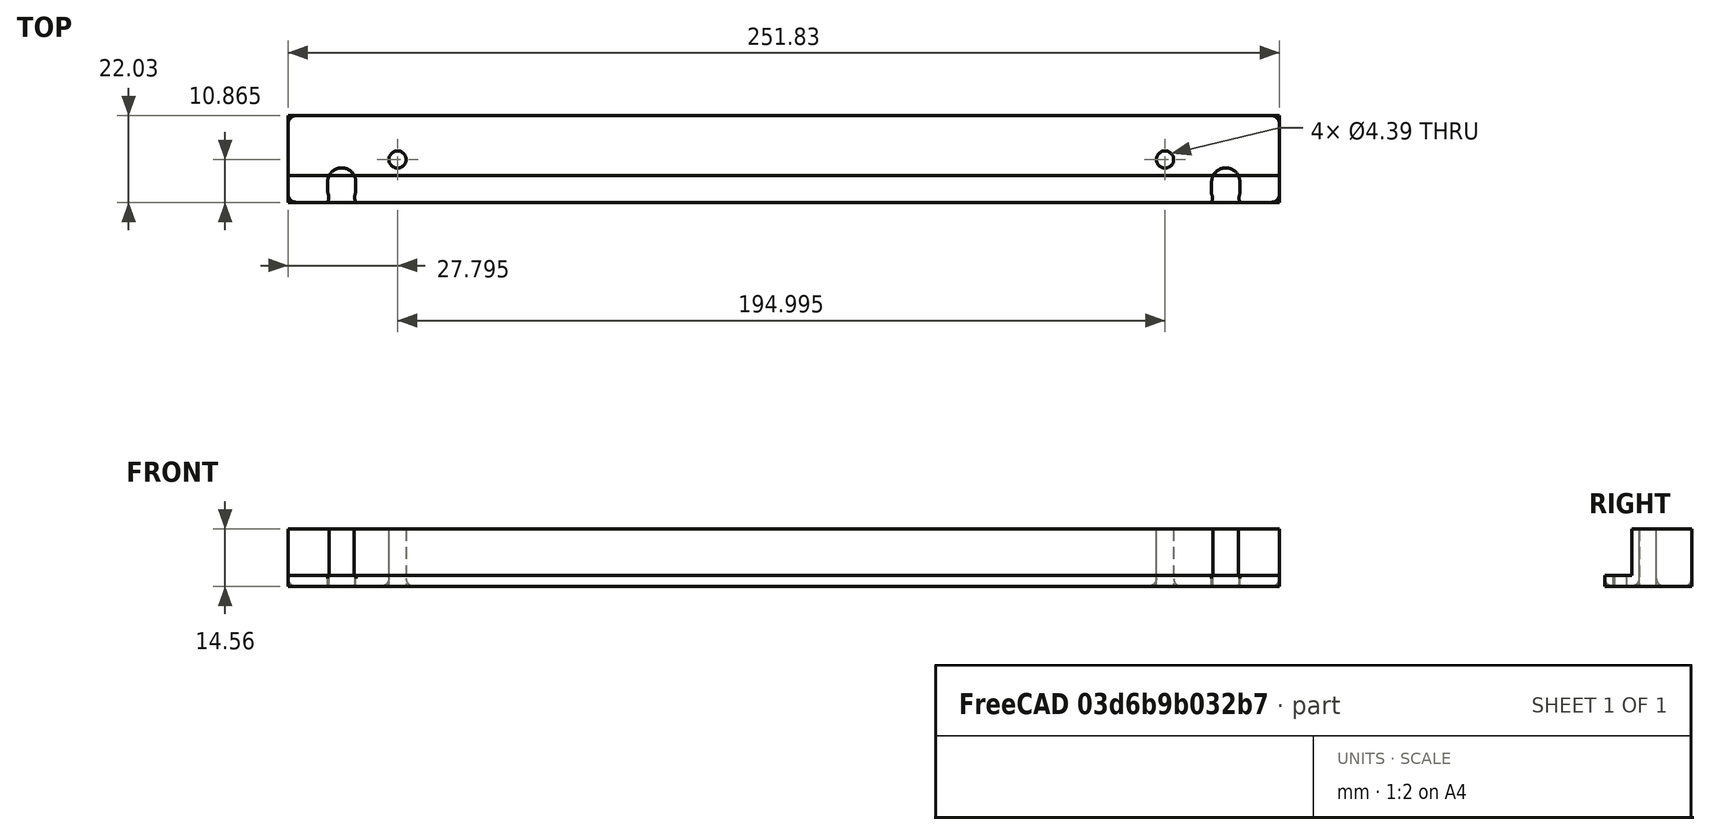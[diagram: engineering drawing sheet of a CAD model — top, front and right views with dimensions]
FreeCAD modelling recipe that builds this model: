
FCSTD DOCUMENT  (FreeCAD 0.19R24276 (Git))
Label: Pieza_Suegros
License: All rights reserved
LicenseURL: http://en.wikipedia.org/wiki/All_rights_reserved
objects: TechDraw::DrawViewDimension×10, Part::Fillet×3, TechDraw::DrawProjGroupItem×3, Part::Box×2, Sketcher::SketchObject×2, PartDesign::Pocket×2, TechDraw::DrawSVGTemplate×2, TechDraw::DrawViewPart×2, TechDraw::DrawPage×2, Part::Cut×1, TechDraw::DrawProjGroup×1, TechDraw::DrawViewAnnotation×1
note: 12 computed .brp shape members not serialized (recipe doc carries the construction recipe); baked Part::Feature solids carry a one-line shape summary decoded from their .brp

FEATURE [Part::Box] Box  label="Cubo"
  AttacherType = Attacher::AttachEngine3D
  Height = 14.56
  Length = 251.83
  Width = 22.03
FEATURE [Part::Box] Box001  label="Cubo001"
  AttacherType = Attacher::AttachEngine3D
  Height = 11.75
  Length = 251.83
  Placement = pos=(0,0,2.81) rot=(0,0,1;0rad)
  Width = 6.77
FEATURE [Part::Cut] Cut
  Base = -> Box
  Tool = -> Box001
FEATURE [Sketcher::SketchObject] Sketch
  ExternalGeometry = -> [Cut]
  FullyConstrained = false
  MapMode = 5
  Placement = pos=(0,0,14.56) rot=(0,0,1;0rad)
  Support = -> [Cut]
  sketch-geometry (6):
    g0: LineSegment StartX=0 StartY=6.77 StartZ=0 EndX=27.795 EndY=6.77 EndZ=0
    g1: LineSegment StartX=27.795 StartY=6.77 StartZ=0 EndX=27.795 EndY=10.865 EndZ=0
    g2: Circle CenterX=27.795 CenterY=10.865 CenterZ=0 NormalX=0 NormalY=0 NormalZ=1 AngleXU=0 Radius=2.195
    g3: LineSegment StartX=251.83 StartY=6.77 StartZ=0 EndX=222.79 EndY=6.77 EndZ=0
    g4: LineSegment StartX=222.79 StartY=6.77 StartZ=0 EndX=222.79 EndY=10.865 EndZ=0
    g5: Circle CenterX=222.79 CenterY=10.865 CenterZ=0 NormalX=0 NormalY=0 NormalZ=1 AngleXU=0 Radius=2.195
  constraints (16):
    c: Coincident(g0,g-3)
    c: Horizontal(g0)
    c: DistanceX(g0) = 27.795
    c: Coincident(g1,g0)
    c: Vertical(g1)
    c: DistanceY(g1) = 4.095
    c: Coincident(g2,g1)
    c: Radius(g2) = 2.195
    c: Coincident(g3,g-4)
    c: Horizontal(g3)
    c: Coincident(g4,g3)
    c: Vertical(g4)
    c: DistanceY(g4) = 4.095
    c: DistanceX(g3) = -29.04
    c: Coincident(g5,g4)
    c: Radius(g5) = 2.195
FEATURE [PartDesign::Pocket] Pocket
  AllowMultiFace = false
  Length = 5
  Length2 = 100
  Profile = -> Sketch
  Type = 1
FEATURE [Sketcher::SketchObject] Sketch001
  ExternalGeometry = -> [Pocket]
  FullyConstrained = false
  MapMode = 5
  Placement = pos=(0,0,0) rot=(1,0,0;3.14159rad)
  Support = -> [Pocket]
  sketch-geometry (23):
    g0: LineSegment StartX=13.62 StartY=0 StartZ=0 EndX=13.62 EndY=-5.14 EndZ=0
    g1: LineSegment StartX=10.0481 StartY=-5.5 StartZ=0 EndX=10.0481 EndY=-2.5 EndZ=0
    g2: LineSegment StartX=13.62 StartY=0 StartZ=0 EndX=17.21 EndY=0 EndZ=0
    g3: LineSegment StartX=17.1919 StartY=-5.5 StartZ=0 EndX=17.1919 EndY=-2.5 EndZ=0
    g4: GeomPoint X=10.0481 Y=-2.5 Z=0
    g5: ArcOfCircle CenterX=7.53364 CenterY=-1.26813 CenterZ=0 NormalX=0 NormalY=0 NormalZ=1 AngleXU=0 Radius=2.8 StartAngle=5.82764 EndAngle=6.75321
    g6: GeomPoint X=17.1919 Y=-2.5 Z=0
    g7: ArcOfCircle CenterX=19.7064 CenterY=-1.26813 CenterZ=0 NormalX=0 NormalY=0 NormalZ=1 AngleXU=0 Radius=2.8 StartAngle=2.67157 EndAngle=3.59714
    g8: LineSegment StartX=238.21 StartY=0 StartZ=0 EndX=238.21 EndY=-5.14 EndZ=0
    g9: ArcOfCircle CenterX=238.21 CenterY=-5.14 CenterZ=0 NormalX=0 NormalY=0 NormalZ=1 AngleXU=0 Radius=3.59 StartAngle=3.14159 EndAngle=6.28319
    g10: LineSegment StartX=241.8 StartY=-5.14 StartZ=0 EndX=241.8 EndY=-2.14 EndZ=0
    g11: GeomPoint X=241.8 Y=-2.14 Z=0
    g12: GeomPoint X=234.62 Y=-2.14 Z=0
    g13: ArcOfCircle CenterX=232.033 CenterY=-1.07 CenterZ=0 NormalX=0 NormalY=0 NormalZ=1 AngleXU=0 Radius=2.8 StartAngle=5.89107 EndAngle=6.6753
    g14: ArcOfCircle CenterX=244.387 CenterY=-1.07 CenterZ=0 NormalX=0 NormalY=0 NormalZ=1 AngleXU=0 Radius=2.8 StartAngle=2.74948 EndAngle=3.53371
    g15: LineSegment StartX=234.62 StartY=-5.14 StartZ=0 EndX=238.21 EndY=-5.14 EndZ=0
    g16: LineSegment StartX=238.21 StartY=-5.14 StartZ=0 EndX=241.8 EndY=-5.14 EndZ=0
    g17: LineSegment StartX=17.21 StartY=0 StartZ=0 EndX=10.03 EndY=0 EndZ=0
    g18: LineSegment StartX=0 StartY=0 StartZ=0 EndX=13.62 EndY=0 EndZ=0
    g19: LineSegment StartX=251.83 StartY=0 StartZ=0 EndX=241.8 EndY=0 EndZ=0
    g20: LineSegment StartX=241.8 StartY=0 StartZ=0 EndX=234.62 EndY=0 EndZ=0
    g21: LineSegment StartX=234.62 StartY=-2.14 StartZ=0 EndX=234.62 EndY=-5.14 EndZ=0
    g22: ArcOfCircle CenterX=13.62 CenterY=-5.14 CenterZ=0 NormalX=0 NormalY=0 NormalZ=1 AngleXU=0 Radius=3.59 StartAngle=3.24204 EndAngle=6.18274
  constraints (66):
    c: Vertical(g0)
    c: DistanceY(g0) = -5.14
    c: Vertical(g1)
    c: Horizontal(g2)
    c: Vertical(g3)
    c: DistanceX(g2) = 3.59
    c: PointOnObject(g4,g1)
    c: Coincident(g5,g4)
    c: Radius(g5) = 2.8
    c: PointOnObject(g1,g5)
    c: DistanceY(g5,g1) = -2.5
    c: DistanceX(g5,g0) = 3.59
    c: PointOnObject(g6,g3)
    c: Coincident(g7,g2)
    c: Coincident(g7,g6)
    c: PointOnObject(g3,g7)
    c: DistanceY(g2,g3) = -2.5
    c: Radius(g7) = 2.8
    c: Vertical(g8)
    c: DistanceY(g8) = -5.14
    c: Vertical(g10)
    c: PointOnObject(g11,g10)
    c: Coincident(g13,g12)
    c: Radius(g13) = 2.8
    c: Coincident(g9,g10)
    c: DistanceY(g11,g9) = -3
    c: Coincident(g14,g10)
    c: Radius(g14) = 2.8
    c: Coincident(g10,g11)
    c: Horizontal(g15)
    c: Coincident(g15,g16)
    c: Coincident(g16,g9)
    c: Horizontal(g16)
    c: DistanceX(g14,g8) = -3.59
    c: Coincident(g17,g2)
    c: Coincident(g17,g5)
    c: Horizontal(g17)
    c: DistanceX(g17) = -7.18
    c: Coincident(g18,g-1)
    c: Coincident(g18,g0)
    c: Horizontal(g18)
    c: DistanceX(g18) = 13.62
    c: Coincident(g2,g0)
    c: Coincident(g19,g-4)
    c: Coincident(g19,g14)
    c: Coincident(g20,g14)
    c: Coincident(g20,g13)
    c: Horizontal(g20)
    c: PointOnObject(g8,g20)
    c: DistanceX(g20) = -7.18
    c: Horizontal(g19)
    c: DistanceX(g19) = -10.03
    c: Coincident(g9,g15)
    c: Coincident(g9,g8)
    c: Coincident(g15,g8)
    c: Coincident(g21,g12)
    c: Coincident(g21,g9)
    c: Vertical(g21)
    c: Radius(g9) = 3.59
    c: Coincident(g22,g0)
    c: Coincident(g22,g3)
    c: Coincident(g22,g1)
    c: Radius(g22) = 3.59
    c: DistanceY(g1) = 3
    c: DistanceY(g3) = 3
    c: Equal(g21,g10)
FEATURE [PartDesign::Pocket] Pocket001
  AllowMultiFace = false
  Length = 5
  Length2 = 100
  Profile = -> Sketch001
  Type = 1
FEATURE [Part::Fillet] Fillet
  Base = -> Pocket001
  Edges = 4 edges r=2: [Edge1,Edge5,Edge25,Edge46]
FEATURE [Part::Fillet] Fillet001
  Base = -> Fillet
  Edges = 2 edges r=2: [Edge35,Edge36]
FEATURE [Part::Fillet] Fillet002
  Base = -> Fillet001
  Edges = 6 edges r=2: [Edge2,Edge5,Edge6,Edge9,Edge10,Edge21]
FEATURE [TechDraw::DrawSVGTemplate] Template
  EditableTexts = Designed_by_Name=<owner>; Drawing_number=001; FC-Date=-; FC-SC=1:2; FC-SH=1/2; FC-Title=KitchenCabinetPiece; Subtitle=Pieza Armario Cocina; Weight=<250gr
  Height = 210
  Orientation = 1
  Width = 297
FEATURE [TechDraw::DrawSVGTemplate] Template001
  EditableTexts = Designed_by_Name=<owner>; Drawing_number=001; FC-Date=-; FC-SC=1:1; FC-SH=2/2; FC-Title=KitchenCabinetPiece; Subtitle=Pieza Armario Cocina; Weight=<250gr
  Height = 210
  Orientation = 1
  Width = 297
FEATURE [TechDraw::DrawViewPart] View
  CoarseView = false
  Direction = (0.577,-0.577,0.577)
  Focus = 100
  HardHidden = false
  IsoCount = 0
  IsoHidden = false
  IsoVisible = false
  LockPosition = false
  Perspective = false
  Rotation = 0
  Scale = 0.5
  ScaleType = 0
  SeamHidden = false
  SeamVisible = true
  SmoothHidden = false
  SmoothVisible = true
  Source = -> [Fillet002]
  X = 229.929
  XDirection = (0.707,0.707,0)
  Y = 131.494
FEATURE [TechDraw::DrawViewPart] View001
  CoarseView = false
  Direction = (0.577,-0.577,0.577)
  Focus = 100
  HardHidden = false
  IsoCount = 0
  IsoHidden = false
  IsoVisible = false
  LockPosition = false
  Perspective = false
  Rotation = 0
  ScaleType = 0
  SeamHidden = false
  SeamVisible = true
  SmoothHidden = false
  SmoothVisible = true
  Source = -> [Fillet002]
  X = 144.994
  XDirection = (0.707,0.707,0)
  Y = 130.325
FEATURE [TechDraw::DrawProjGroupItem] ProjItem  label="Front"
  CoarseView = false
  Direction = (0,-1,0)
  Focus = 100
  HardHidden = false
  IsoCount = 0
  IsoHidden = false
  IsoVisible = false
  LockPosition = true
  Perspective = false
  Rotation = 0
  RotationVector = (1,0,0)
  Scale = 0.5
  ScaleType = 2
  SeamHidden = false
  SeamVisible = true
  SmoothHidden = false
  SmoothVisible = true
  Source = -> [Fillet002]
  Type = 0
  X = 0
  XDirection = (1,0,0)
  Y = 0
FEATURE [TechDraw::DrawProjGroupItem] ProjItem001  label="Right"
  CoarseView = false
  Direction = (1,-1e-16,0)
  Focus = 100
  HardHidden = false
  IsoCount = 0
  IsoHidden = false
  IsoVisible = false
  LockPosition = false
  Perspective = false
  Rotation = 0
  RotationVector = (1,0,0)
  ScaleType = 2
  SeamHidden = false
  SeamVisible = true
  SmoothHidden = false
  SmoothVisible = true
  Source = -> [Fillet002]
  Type = 2
  X = -83.465
  XDirection = (1e-16,1,0)
  Y = 0
FEATURE [TechDraw::DrawProjGroupItem] ProjItem002  label="Top"
  CoarseView = false
  Direction = (0,0,1)
  Focus = 100
  HardHidden = false
  IsoCount = 0
  IsoHidden = false
  IsoVisible = false
  LockPosition = false
  Perspective = false
  Rotation = 0
  RotationVector = (1,0,0)
  ScaleType = 2
  SeamHidden = false
  SeamVisible = true
  SmoothHidden = false
  SmoothVisible = true
  Source = -> [Fillet002]
  Type = 4
  X = 0
  XDirection = (1,0,0)
  Y = -26.015
FEATURE [TechDraw::DrawProjGroup] ProjGroup
  Anchor = -> ProjItem
  AutoDistribute = true
  LockPosition = false
  ProjectionType = 0
  Rotation = 0
  Scale = 0.5
  ScaleType = 2
  Source = -> [Fillet002]
  Views = -> [ProjItem,ProjItem001,ProjItem002]
  X = 106.812
  Y = 145.13
  spacingX = 15
  spacingY = 15
FEATURE [TechDraw::DrawViewDimension] Dimension
  Arbitrary = false
  ArbitraryTolerances = false
  EqualTolerance = true
  FormatSpec = %.2f
  FormatSpecOverTolerance = %+.2f
  FormatSpecUnderTolerance = %+.2f
  Inverted = false
  LockPosition = false
  MeasureType = 1
  OverTolerance = 0
  References2D = -> [ProjItem002]
  Rotation = 0
  ScaleType = 0
  TheoreticalExact = false
  Type = 2
  UnderTolerance = 0
  X = 61.5575
  Y = -17.6
FEATURE [TechDraw::DrawViewDimension] Dimension001
  Arbitrary = false
  ArbitraryTolerances = false
  EqualTolerance = true
  FormatSpec = %.2f
  FormatSpecOverTolerance = %+.2f
  FormatSpecUnderTolerance = %+.2f
  Inverted = false
  LockPosition = false
  MeasureType = 1
  OverTolerance = 0
  References2D = -> [ProjItem002]
  Rotation = 0
  ScaleType = 0
  TheoreticalExact = false
  Type = 1
  UnderTolerance = 0
  X = -3.83297
  Y = 14.2027
FEATURE [TechDraw::DrawViewDimension] Dimension002
  Arbitrary = false
  ArbitraryTolerances = false
  EqualTolerance = true
  FormatSpec = %.2f
  FormatSpecOverTolerance = %+.2f
  FormatSpecUnderTolerance = %+.2f
  Inverted = false
  LockPosition = false
  MeasureType = 1
  OverTolerance = 0
  References2D = -> [ProjItem001]
  Rotation = 0
  ScaleType = 0
  TheoreticalExact = false
  Type = 2
  UnderTolerance = 0
  X = 6.56193
  Y = 22.0117
FEATURE [TechDraw::DrawPage] Page  label="Vistas"
  KeepUpdated = true
  NextBalloonIndex = 1
  ProjectionType = 0
  Template = -> Template
  Views = -> [View,ProjGroup,Dimension,Dimension001,Dimension002]
FEATURE [TechDraw::DrawViewDimension] Dimension003
  Arbitrary = false
  ArbitraryTolerances = false
  EqualTolerance = true
  FormatSpec = ⌀%.2f
  FormatSpecOverTolerance = %+.2f
  FormatSpecUnderTolerance = %+.2f
  Inverted = false
  LockPosition = false
  MeasureType = 1
  OverTolerance = 0
  References2D = -> [View001]
  Rotation = 0
  ScaleType = 0
  TheoreticalExact = false
  Type = 5
  UnderTolerance = 0
  X = 38.4205
  Y = -20.2394
FEATURE [TechDraw::DrawViewDimension] Dimension004
  Arbitrary = false
  ArbitraryTolerances = false
  EqualTolerance = true
  FormatSpec = ⌀%.2f
  FormatSpecOverTolerance = %+.2f
  FormatSpecUnderTolerance = %+.2f
  Inverted = false
  LockPosition = false
  MeasureType = 1
  OverTolerance = 0
  References2D = -> [View001]
  Rotation = 0
  ScaleType = 0
  TheoreticalExact = false
  Type = 5
  UnderTolerance = 0
  X = 32.7603
  Y = -40.9933
FEATURE [TechDraw::DrawViewDimension] Dimension005
  Arbitrary = false
  ArbitraryTolerances = false
  EqualTolerance = true
  FormatSpec = %.2f
  FormatSpecOverTolerance = %+.2f
  FormatSpecUnderTolerance = %+.2f
  Inverted = false
  LockPosition = false
  MeasureType = 1
  OverTolerance = 0
  References2D = -> [View001]
  Rotation = 0
  ScaleType = 0
  TheoreticalExact = false
  Type = 0
  UnderTolerance = 0
  X = 96.7569
  Y = -21.9618
FEATURE [TechDraw::DrawViewDimension] Dimension006
  Arbitrary = false
  ArbitraryTolerances = false
  EqualTolerance = true
  FormatSpec = %.2f
  FormatSpecOverTolerance = %+.2f
  FormatSpecUnderTolerance = %+.2f
  Inverted = false
  LockPosition = false
  MeasureType = 1
  OverTolerance = 0
  References2D = -> [View001]
  Rotation = 0
  ScaleType = 0
  TheoreticalExact = false
  Type = 0
  UnderTolerance = 0
  X = 11.2612
  Y = -39.6864
FEATURE [TechDraw::DrawViewDimension] Dimension007
  Arbitrary = false
  ArbitraryTolerances = false
  EqualTolerance = true
  FormatSpec = %.2f
  FormatSpecOverTolerance = %+.2f
  FormatSpecUnderTolerance = %+.2f
  Inverted = false
  LockPosition = false
  MeasureType = 1
  OverTolerance = 0
  References2D = -> [View001]
  Rotation = 0
  ScaleType = 0
  TheoreticalExact = false
  Type = 0
  UnderTolerance = 0
  X = 110.854
  Y = 0.152332
FEATURE [TechDraw::DrawViewDimension] Dimension008
  Arbitrary = false
  ArbitraryTolerances = false
  EqualTolerance = true
  FormatSpec = %.2f
  FormatSpecOverTolerance = %+.2f
  FormatSpecUnderTolerance = %+.2f
  Inverted = false
  LockPosition = false
  MeasureType = 1
  OverTolerance = 0
  References2D = -> [View001]
  Rotation = 0
  ScaleType = 0
  TheoreticalExact = false
  Type = 1
  UnderTolerance = 0
  X = -119.982
  Y = 55.3368
FEATURE [TechDraw::DrawViewDimension] Dimension009
  Arbitrary = false
  ArbitraryTolerances = false
  EqualTolerance = true
  FormatSpec = ⌀%.2f
  FormatSpecOverTolerance = %+.2f
  FormatSpecUnderTolerance = %+.2f
  Inverted = false
  LockPosition = false
  MeasureType = 1
  OverTolerance = 0
  References2D = -> [View001]
  Rotation = 0
  ScaleType = 0
  TheoreticalExact = false
  Type = 5
  UnderTolerance = 0
  X = -67.4841
  Y = 60.9079
FEATURE [TechDraw::DrawViewAnnotation] Annotation
  Font = osifont
  LineSpace = 80
  LockPosition = false
  MaxWidth = -1
  Rotation = 0
  ScaleType = 0
  Text = Aproximate measurements: | Check with 3D piece
  TextSize = 5
  TextStyle = 0
  X = 86.1
  Y = 90.6
FEATURE [TechDraw::DrawPage] Page001  label="Cotas"
  KeepUpdated = true
  NextBalloonIndex = 1
  ProjectionType = 0
  Template = -> Template001
  Views = -> [View001,Dimension003,Dimension004,Dimension005,Dimension006,Dimension007,Dimension008,Dimension009,Annotation]
